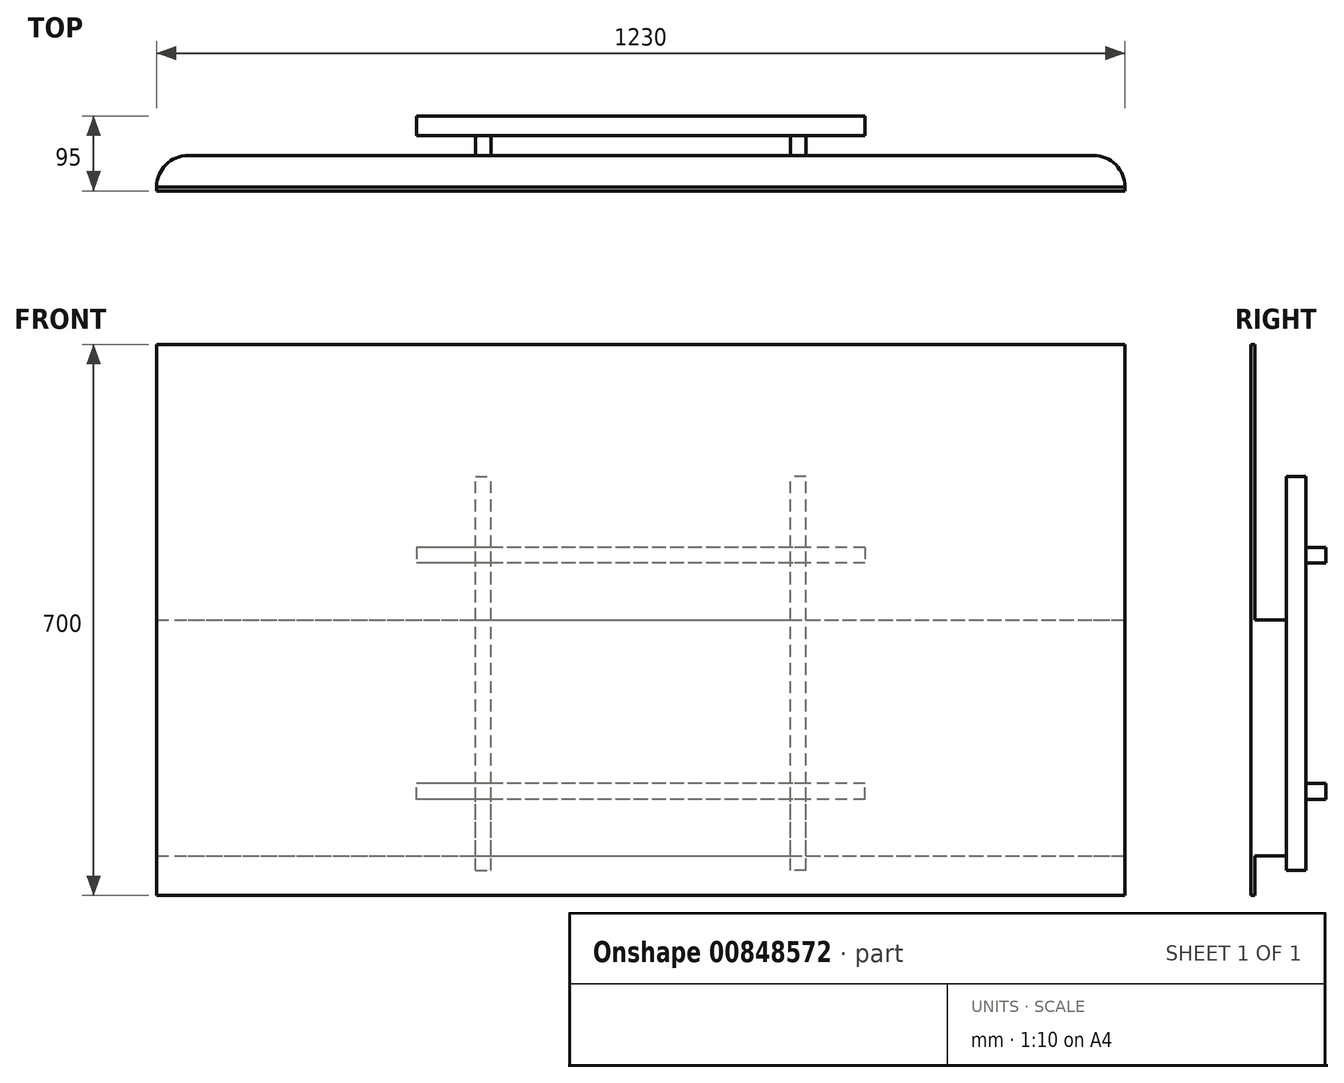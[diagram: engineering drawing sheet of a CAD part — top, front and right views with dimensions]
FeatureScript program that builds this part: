
annotation { "Feature Type Name" : "Feature", "Feature Type Description" : "" }
export const myFeature = defineFeature(function(context is Context, id is Id, definition is map)
    precondition{}
    {
        {
            var Q0;
            Q0=qCreatedBy(makeId("Front.planeOp"),FACE);
            var sketch = newSketch(context, id + "F0", { "sketchPlane" : qUnion([Q0])});
            skLineSegment(sketch, "E0.bottom", {"start": v(615, 350) * mm, "end": v(-615, 350) * mm});
            skLineSegment(sketch, "E0.top", {"start": v(615, -350) * mm, "end": v(-615, -350) * mm});
            skLineSegment(sketch, "E0.left", {"start": v(615, 350) * mm, "end": v(615, -350) * mm});
            skLineSegment(sketch, "E0.right", {"start": v(-615, 350) * mm, "end": v(-615, -350) * mm});
            skPoint(sketch, "E0.middle", {"position": v(0, 0) * mm});
            skSolve(sketch);
        }
        {
            var Q0;
            Q0 = qSketchRegion(id + "F0", true);
            extrude(context, id + "F1", {"entities" : qUnion([Q0]), "depth" : 5 * mm, "offsetDistance" : 25 * mm});
        }
        {
            var Q0;
            Q0=makeQuery(id+"F1.opExtrude","CAP_FACE",FACE,{"disambiguationData":[OSD([sQuery(id+"F0.wireOp",EDGE,"E0.bottom"),sQuery(id+"F0.wireOp",EDGE,"E0.top"),sQuery(id+"F0.wireOp",EDGE,"E0.left"),sQuery(id+"F0.wireOp",EDGE,"E0.right")])],"isStart":true});
            var sketch = newSketch(context, id + "F2", { "sketchPlane" : qUnion([Q0])});
            skLineSegment(sketch, "E1.bottom", {"start": v(615, 0) * mm, "end": v(-615, 0) * mm});
            skLineSegment(sketch, "E1.top", {"start": v(615, -300) * mm, "end": v(-615, -300) * mm});
            skLineSegment(sketch, "E1.left", {"start": v(615, 0) * mm, "end": v(615, -300) * mm});
            skLineSegment(sketch, "E1.right", {"start": v(-615, 0) * mm, "end": v(-615, -300) * mm});
            skPoint(sketch, "E1.middle", {"position": v(0, -150) * mm});
            skSolve(sketch);
        }
        {
            var Q0;
            Q0 = qSketchRegion(id + "F2", true);
            extrude(context, id + "F3", {"entities" : qUnion([Q0]), "operationType" : NewBodyOperationType.ADD, "depth" : 40 * mm, "offsetDistance" : 25 * mm});
        }
        {
            var Q0;
            Q0=makeQuery(id+"F3.opExtrude","CAP_EDGE",EDGE,{"disambiguationData":[OSD([sQuery(id+"F2.wireOp",EDGE,"E1.right")])],"isStart":false});
            var Q1;
            Q1=makeQuery(id+"F3.opExtrude","CAP_EDGE",EDGE,{"disambiguationData":[OSD([sQuery(id+"F2.wireOp",EDGE,"E1.left")])],"isStart":false});
            fillet(context, id + "F4", {"entities" : qUnion([Q0, Q1]), "radius" : 40 * mm, "tangentPropagation" : true, "allowEdgeOverflow" : false});
        }
        {
            var Q0;
            Q0=makeQuery(id+"F3.opExtrude","CAP_FACE",FACE,{"disambiguationData":[OSD([sQuery(id+"F2.wireOp",EDGE,"E1.bottom"),sQuery(id+"F2.wireOp",EDGE,"E1.top"),sQuery(id+"F2.wireOp",EDGE,"E1.left"),sQuery(id+"F2.wireOp",EDGE,"E1.right")])],"isStart":false});
            var sketch = newSketch(context, id + "F5", { "sketchPlane" : qUnion([Q0])});
            skLineSegment(sketch, "E2", {"start": v(-200, -317.9) * mm, "end": v(-200, 182.1) * mm, "construction": true});
            skLineSegment(sketch, "E3.0", {"start": v(-190, -317.9) * mm, "end": v(-190, 182.1) * mm});
            skLineSegment(sketch, "E4.0", {"start": v(-210, -317.9) * mm, "end": v(-210, 182.1) * mm});
            skLineSegment(sketch, "E5", {"start": v(-210, 182.1) * mm, "end": v(-190, 182.1) * mm});
            skLineSegment(sketch, "E6", {"start": v(-210, -317.9) * mm, "end": v(-190, -317.9) * mm});
            skLineSegment(sketch, "E7", {"start": v(0, -13.33) * mm, "end": v(0, -211.43) * mm, "construction": true});
            skLineSegment(sketch, "E8.MirrorCS", {"start": v(-190, -317.9) * mm, "end": v(-210, -317.9) * mm});
            skLineSegment(sketch, "E9.MirrorCS", {"start": v(-190, 182.1) * mm, "end": v(-210, 182.1) * mm});
            skLineSegment(sketch, "E10.MirrorCS", {"start": v(210, -317.9) * mm, "end": v(190, -317.9) * mm});
            skLineSegment(sketch, "E11.MirrorCS", {"start": v(210, 182.1) * mm, "end": v(190, 182.1) * mm});
            skLineSegment(sketch, "E12.MirrorCS", {"start": v(190, -317.9) * mm, "end": v(210, -317.9) * mm});
            skLineSegment(sketch, "E13.MirrorCS", {"start": v(190, 182.1) * mm, "end": v(210, 182.1) * mm});
            skLineSegment(sketch, "E14.MirrorCS", {"start": v(190, -317.9) * mm, "end": v(190, 182.1) * mm});
            skLineSegment(sketch, "E15.MirrorCS", {"start": v(210, -317.9) * mm, "end": v(210, 182.1) * mm});
            skLineSegment(sketch, "E16.MirrorCS", {"start": v(200, -317.9) * mm, "end": v(200, 182.1) * mm, "construction": true});
            skSolve(sketch);
        }
        {
            var Q0;
            Q0 = qSketchRegion(id + "F5", true);
            extrude(context, id + "F6", {"entities" : qUnion([Q0]), "operationType" : NewBodyOperationType.ADD, "depth" : 25 * mm, "offsetDistance" : 25 * mm});
        }
        {
            var Q0;
            Q0=makeQuery(id+"F6.opExtrude","CAP_FACE",FACE,{"disambiguationData":[OSD([sQuery(id+"F5.wireOp",EDGE,"E8.MirrorCS"),sQuery(id+"F5.wireOp",EDGE,"E9.MirrorCS"),sQuery(id+"F5.wireOp",EDGE,"E4.0"),sQuery(id+"F5.wireOp",EDGE,"E3.0")])],"isStart":false});
            var sketch = newSketch(context, id + "F7", { "sketchPlane" : qUnion([Q0])});
            skLineSegment(sketch, "E17", {"start": v(-285, 82.1) * mm, "end": v(285, 82.1) * mm, "construction": true});
            skLineSegment(sketch, "E18.0", {"start": v(-285, 92.1) * mm, "end": v(285, 92.1) * mm});
            skLineSegment(sketch, "E19.MirrorCS", {"start": v(-285, 72.1) * mm, "end": v(285, 72.1) * mm});
            skLineSegment(sketch, "E20", {"start": v(-285, 92.1) * mm, "end": v(-285, 72.1) * mm});
            skLineSegment(sketch, "E21", {"start": v(285, 92.1) * mm, "end": v(285, 72.1) * mm});
            skLineSegment(sketch, "E22.0", {"start": v(190, -317.9) * mm, "end": v(190, 182.1) * mm, "construction": true});
            skLineSegment(sketch, "E23", {"start": v(190, -67.9) * mm, "end": v(-60.43, -67.9) * mm, "construction": true});
            skLineSegment(sketch, "E24.MirrorCS", {"start": v(-285, -227.9) * mm, "end": v(-285, -207.9) * mm});
            skLineSegment(sketch, "E25.MirrorCS", {"start": v(285, -227.9) * mm, "end": v(285, -207.9) * mm});
            skLineSegment(sketch, "E26.MirrorCS", {"start": v(-285, -207.9) * mm, "end": v(285, -207.9) * mm});
            skLineSegment(sketch, "E27.MirrorCS", {"start": v(-285, -217.9) * mm, "end": v(285, -217.9) * mm, "construction": true});
            skLineSegment(sketch, "E28.MirrorCS", {"start": v(-285, -227.9) * mm, "end": v(285, -227.9) * mm});
            skSolve(sketch);
        }
        {
            var Q0;
            Q0 = qSketchRegion(id + "F7", true);
            extrude(context, id + "F8", {"entities" : qUnion([Q0]), "operationType" : NewBodyOperationType.ADD, "depth" : 25 * mm, "offsetDistance" : 25 * mm});
        }
    });
